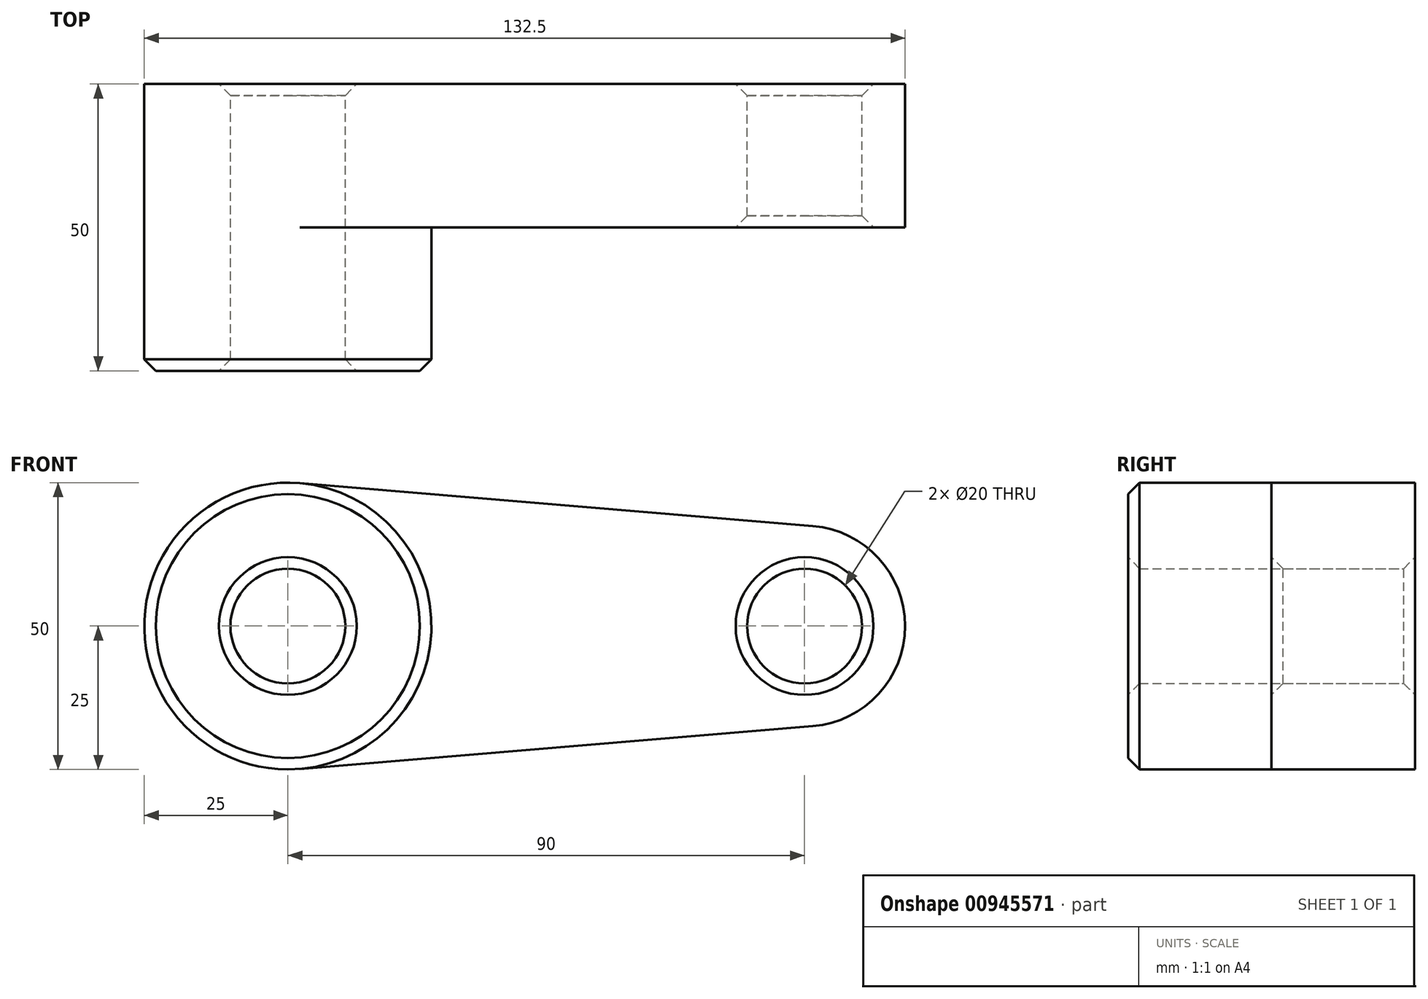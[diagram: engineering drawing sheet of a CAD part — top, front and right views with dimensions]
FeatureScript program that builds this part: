
annotation { "Feature Type Name" : "Feature", "Feature Type Description" : "" }
export const myFeature = defineFeature(function(context is Context, id is Id, definition is map)
    precondition{}
    {
        {
            var Q0;
            Q0=qCreatedBy(makeId("Front.planeOp"),FACE);
            var sketch = newSketch(context, id + "F0", { "sketchPlane" : qUnion([Q0])});
            skCircle(sketch, "E0", {"center": v(0, 0) * mm, "radius": 25 * mm});
            skCircle(sketch, "E1", {"center": v(90, 0) * mm, "radius": 17.5 * mm});
            skLineSegment(sketch, "E2", {"start": v(2.08, -24.91) * mm, "end": v(91.46, -17.44) * mm});
            skLineSegment(sketch, "E3", {"start": v(2.08, 24.91) * mm, "end": v(91.46, 17.44) * mm});
            skCircle(sketch, "E4", {"center": v(0, 0) * mm, "radius": 10 * mm});
            skCircle(sketch, "E5", {"center": v(90, 0) * mm, "radius": 10 * mm});
            skSolve(sketch);
        }
        {
            var Q0;
            Q0 = qSketchRegion(id + "F0", true);
            extrude(context, id + "F1", {"entities" : qUnion([Q0]), "depth" : 25 * mm, "offsetDistance" : 25 * mm});
        }
        {
            var Q0;
            Q0=makeQuery(id+"F0.imprint","IMPRINT",FACE,{"disambiguationData":[TD([[makeQuery(id+"F0.imprint","IMPRINT",EDGE,{"derivedFrom":sQuery(id+"F0.wireOp",EDGE,"E4")}),-1.0]])]});
            extrude(context, id + "F2", {"entities" : qUnion([Q0]), "operationType" : NewBodyOperationType.ADD, "depth" : 50 * mm, "offsetDistance" : 25 * mm});
        }
        {
            var Q0;
            Q0=makeQuery(id+"F2.opExtrude","CAP_EDGE",EDGE,{"disambiguationData":[OSD([sQuery(id+"F0.wireOp",EDGE,"E0")])],"isStart":false});
            var Q1;
            Q1=makeQuery(id+"F2.opExtrude","CAP_EDGE",EDGE,{"disambiguationData":[OSD([sQuery(id+"F0.wireOp",EDGE,"E4")])],"isStart":false});
            var Q2;
            Q2=makeQuery(id+"F1.opExtrude","CAP_EDGE",EDGE,{"disambiguationData":[OSD([sQuery(id+"F0.wireOp",EDGE,"E5")])],"isStart":false});
            chamfer(context, id + "F3", {"entities" : qUnion([Q0, Q1, Q2]), "width" : 2 * mm, "tangentPropagation" : true});
        }
        {
            var Q0;
            Q0=makeQuery(id+"F1.opExtrude","CAP_EDGE",EDGE,{"disambiguationData":[OSD([sQuery(id+"F0.wireOp",EDGE,"E4")])],"isStart":true});
            var Q1;
            Q1=makeQuery(id+"F1.opExtrude","CAP_EDGE",EDGE,{"disambiguationData":[OSD([sQuery(id+"F0.wireOp",EDGE,"E5")])],"isStart":true});
            chamfer(context, id + "F4", {"entities" : qUnion([Q0, Q1]), "width" : 2 * mm, "tangentPropagation" : true});
        }
    });
